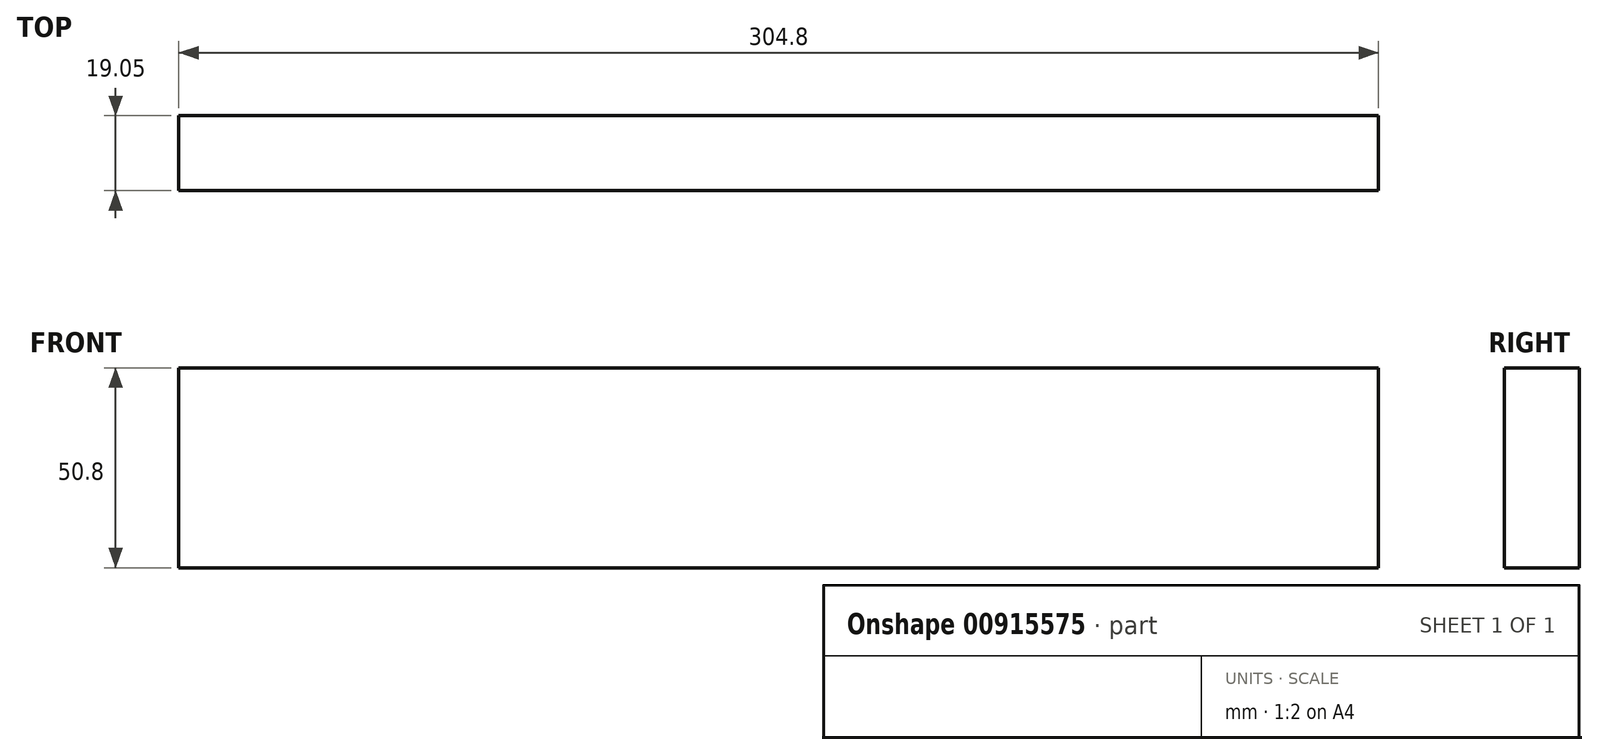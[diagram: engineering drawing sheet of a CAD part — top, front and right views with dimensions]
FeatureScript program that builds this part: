
annotation { "Feature Type Name" : "Feature", "Feature Type Description" : "" }
export const myFeature = defineFeature(function(context is Context, id is Id, definition is map)
    precondition{}
    {
        {
            var Q0;
            Q0=qCreatedBy(makeId("Front.planeOp"),FACE);
            var sketch = newSketch(context, id + "F0", { "sketchPlane" : qUnion([Q0])});
            skLineSegment(sketch, "E0.bottom", {"start": v(152.4, 25.4) * mm, "end": v(-152.4, 25.4) * mm});
            skLineSegment(sketch, "E0.top", {"start": v(152.4, -25.4) * mm, "end": v(-152.4, -25.4) * mm});
            skLineSegment(sketch, "E0.left", {"start": v(152.4, 25.4) * mm, "end": v(152.4, -25.4) * mm});
            skLineSegment(sketch, "E0.right", {"start": v(-152.4, 25.4) * mm, "end": v(-152.4, -25.4) * mm});
            skPoint(sketch, "E0.middle", {"position": v(0, 0) * mm});
            skSolve(sketch);
        }
        {
            var Q0;
            Q0=makeQuery(id+"F0.imprint","IMPRINT",FACE,{"disambiguationData":[TD([[makeQuery(id+"F0.imprint","IMPRINT",EDGE,{"derivedFrom":sQuery(id+"F0.wireOp",EDGE,"E0.bottom")}),1.0]])]});
            extrude(context, id + "F1", {"entities" : qUnion([Q0]), "depth" : 19.05 * mm, "offsetDistance" : 25.4 * mm});
        }
    });
